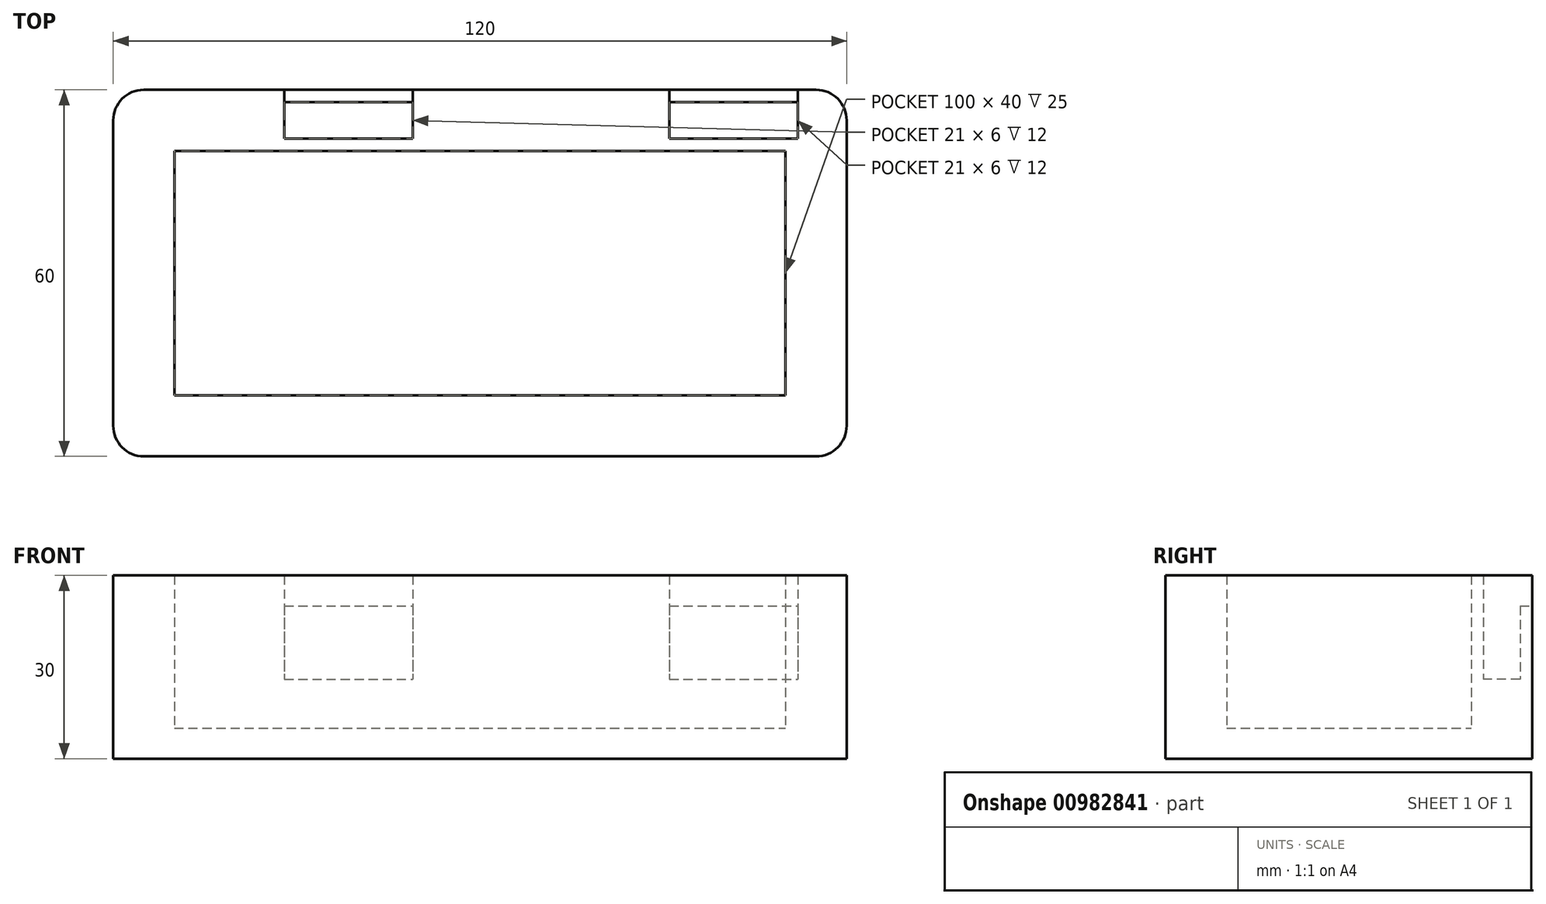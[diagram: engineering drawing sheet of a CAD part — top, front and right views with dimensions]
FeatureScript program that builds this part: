
annotation { "Feature Type Name" : "Feature", "Feature Type Description" : "" }
export const myFeature = defineFeature(function(context is Context, id is Id, definition is map)
    precondition{}
    {
        {
            var Q0;
            Q0=qCreatedBy(makeId("Top.planeOp"),FACE);
            var sketch = newSketch(context, id + "F0", { "sketchPlane" : qUnion([Q0])});
            skLineSegment(sketch, "E0.bottom", {"start": v(0, 0) * mm, "end": v(120, 0) * mm});
            skLineSegment(sketch, "E0.top", {"start": v(0, 60) * mm, "end": v(120, 60) * mm});
            skLineSegment(sketch, "E0.left", {"start": v(0, 0) * mm, "end": v(0, 60) * mm});
            skLineSegment(sketch, "E0.right", {"start": v(120, 0) * mm, "end": v(120, 60) * mm});
            skLineSegment(sketch, "E1.bottom", {"start": v(10, 10) * mm, "end": v(110, 10) * mm});
            skLineSegment(sketch, "E1.top", {"start": v(10, 50) * mm, "end": v(110, 50) * mm});
            skLineSegment(sketch, "E1.left", {"start": v(10, 10) * mm, "end": v(10, 50) * mm});
            skLineSegment(sketch, "E1.right", {"start": v(110, 10) * mm, "end": v(110, 50) * mm});
            skLineSegment(sketch, "E2.bottom", {"start": v(28, 58) * mm, "end": v(49, 58) * mm});
            skLineSegment(sketch, "E2.top", {"start": v(28, 52) * mm, "end": v(49, 52) * mm});
            skLineSegment(sketch, "E2.left", {"start": v(28, 58) * mm, "end": v(28, 52) * mm});
            skLineSegment(sketch, "E2.right", {"start": v(49, 58) * mm, "end": v(49, 52) * mm});
            skLineSegment(sketch, "E3.bottom", {"start": v(91, 58) * mm, "end": v(112, 58) * mm});
            skLineSegment(sketch, "E3.top", {"start": v(91, 52) * mm, "end": v(112, 52) * mm});
            skLineSegment(sketch, "E3.left", {"start": v(91, 58) * mm, "end": v(91, 52) * mm});
            skLineSegment(sketch, "E3.right", {"start": v(112, 58) * mm, "end": v(112, 52) * mm});
            skLineSegment(sketch, "E4", {"start": v(10, 10) * mm, "end": v(10, 0) * mm, "construction": true});
            skLineSegment(sketch, "E5", {"start": v(10, 10) * mm, "end": v(0, 10) * mm, "construction": true});
            skLineSegment(sketch, "E6", {"start": v(110, 10) * mm, "end": v(120, 10) * mm, "construction": true});
            skLineSegment(sketch, "E7", {"start": v(10, 50) * mm, "end": v(10, 60) * mm, "construction": true});
            skLineSegment(sketch, "E8", {"start": v(28, 52) * mm, "end": v(28, 50) * mm, "construction": true});
            skLineSegment(sketch, "E9", {"start": v(91, 58) * mm, "end": v(91, 60) * mm});
            skLineSegment(sketch, "E10", {"start": v(49, 52) * mm, "end": v(70, 52) * mm, "construction": true});
            skLineSegment(sketch, "E11", {"start": v(70, 52) * mm, "end": v(91, 52) * mm, "construction": true});
            skLineSegment(sketch, "E12", {"start": v(112, 58) * mm, "end": v(112, 60) * mm});
            skLineSegment(sketch, "E13", {"start": v(49, 58) * mm, "end": v(49, 60) * mm});
            skLineSegment(sketch, "E14", {"start": v(28, 58) * mm, "end": v(28, 60) * mm});
            skPoint(sketch, "E15", {"position": v(38.5, 58) * mm});
            skPoint(sketch, "E16", {"position": v(101.5, 58) * mm});
            skLineSegment(sketch, "E17", {"start": v(0, 75.53) * mm, "end": v(18.5, 75.53) * mm, "construction": true});
            skLineSegment(sketch, "E18", {"start": v(8, 64.83) * mm, "end": v(29, 64.83) * mm, "construction": true});
            skPoint(sketch, "E19", {"position": v(18.5, 64.83) * mm});
            skLineSegment(sketch, "E20", {"start": v(120, 75.53) * mm, "end": v(101.5, 75.53) * mm, "construction": true});
            skLineSegment(sketch, "E21", {"start": v(38.5, 68.5) * mm, "end": v(18.5, 68.5) * mm, "construction": true});
            skSolve(sketch);
        }
        {
            var Q0;
            Q0=makeQuery(id+"F0.imprint","IMPRINT",FACE,{"disambiguationData":[TD([[makeQuery(id+"F0.imprint","IMPRINT",EDGE,{"derivedFrom":sQuery(id+"F0.wireOp",EDGE,"E0.bottom")}),1.0]])]});
            extrude(context, id + "F1", {"entities" : qUnion([Q0]), "depth" : 30 * mm, "offsetDistance" : 25 * mm});
        }
        {
            var Q0;
            Q0=makeQuery(id+"F0.imprint","IMPRINT",FACE,{"disambiguationData":[TD([[makeQuery(id+"F0.imprint","IMPRINT",EDGE,{"derivedFrom":sQuery(id+"F0.wireOp",EDGE,"E1.bottom")}),1.0]])]});
            extrude(context, id + "F2", {"entities" : qUnion([Q0]), "operationType" : NewBodyOperationType.ADD, "depth" : 5 * mm, "offsetDistance" : 25 * mm});
        }
        {
            var Q0;
            Q0=makeQuery(id+"F0.imprint","IMPRINT",FACE,{"disambiguationData":[TD([[makeQuery(id+"F0.imprint","IMPRINT",EDGE,{"derivedFrom":sQuery(id+"F0.wireOp",EDGE,"E2.bottom")}),-1.0]])]});
            var Q1;
            Q1=makeQuery(id+"F0.imprint","IMPRINT",FACE,{"disambiguationData":[TD([[makeQuery(id+"F0.imprint","IMPRINT",EDGE,{"derivedFrom":sQuery(id+"F0.wireOp",EDGE,"E3.bottom")}),-1.0]])]});
            extrude(context, id + "F3", {"entities" : qUnion([Q0, Q1]), "operationType" : NewBodyOperationType.ADD, "depth" : 13 * mm, "offsetDistance" : 25 * mm});
        }
        {
            var Q0;
            Q0=makeQuery(id+"F0.imprint","IMPRINT",FACE,{"disambiguationData":[TD([[makeQuery(id+"F0.imprint","IMPRINT",EDGE,{"derivedFrom":sQuery(id+"F0.wireOp",EDGE,"E2.bottom")}),1.0]])]});
            var Q1;
            Q1=makeQuery(id+"F0.imprint","IMPRINT",FACE,{"disambiguationData":[TD([[makeQuery(id+"F0.imprint","IMPRINT",EDGE,{"derivedFrom":sQuery(id+"F0.wireOp",EDGE,"E3.bottom")}),1.0]])]});
            extrude(context, id + "F4", {"entities" : qUnion([Q0, Q1]), "operationType" : NewBodyOperationType.ADD, "depth" : 25 * mm, "offsetDistance" : 25 * mm});
        }
        {
            var Q0;
            Q0=makeQuery(id+"F1.opExtrude","SWEPT_EDGE",EDGE,{"disambiguationData":[OSD([sQuery(id+"F0.wireOp",EDGE,"E0.bottom"),sQuery(id+"F0.wireOp",EDGE,"E0.left")])]});
            var Q1;
            Q1=makeQuery(id+"F1.opExtrude","SWEPT_EDGE",EDGE,{"disambiguationData":[OSD([sQuery(id+"F0.wireOp",EDGE,"E0.bottom"),sQuery(id+"F0.wireOp",EDGE,"E0.right")])]});
            var Q2;
            Q2=makeQuery(id+"F1.opExtrude","SWEPT_EDGE",EDGE,{"disambiguationData":[OSD([sQuery(id+"F0.wireOp",EDGE,"E0.top"),sQuery(id+"F0.wireOp",EDGE,"E0.right")])]});
            var Q3;
            Q3=makeQuery(id+"F1.opExtrude","SWEPT_EDGE",EDGE,{"disambiguationData":[OSD([sQuery(id+"F0.wireOp",EDGE,"E0.top"),sQuery(id+"F0.wireOp",EDGE,"E0.left")])]});
            fillet(context, id + "F5", {"entities" : qUnion([Q0, Q1, Q2, Q3]), "radius" : 5 * mm, "tangentPropagation" : true, "allowEdgeOverflow" : false});
        }
    });
